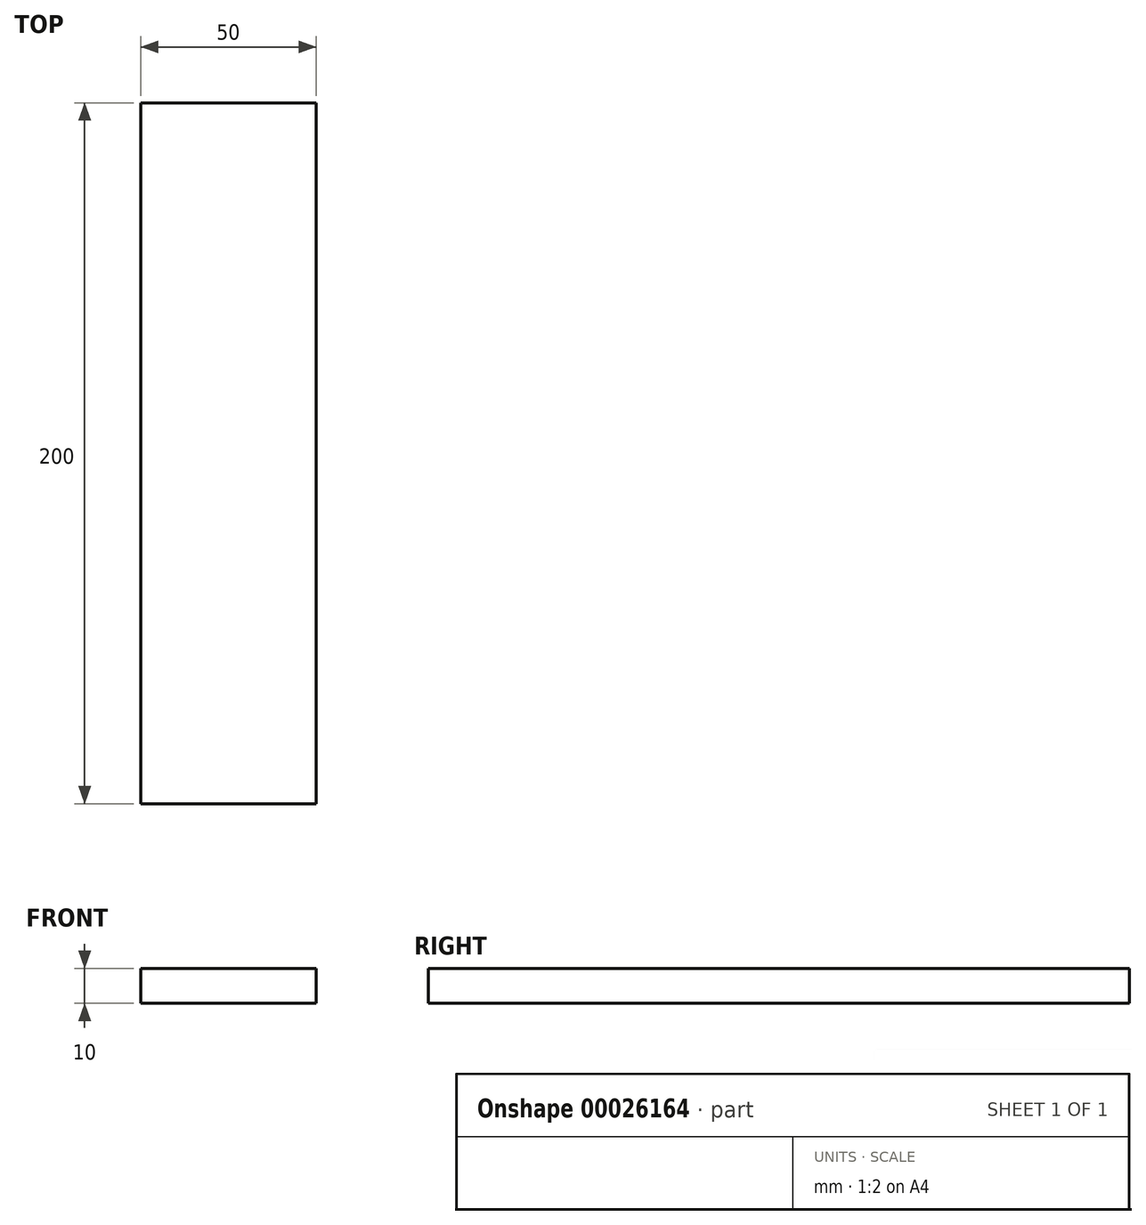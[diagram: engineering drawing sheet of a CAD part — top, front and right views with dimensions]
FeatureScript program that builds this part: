
annotation { "Feature Type Name" : "Feature", "Feature Type Description" : "" }
export const myFeature = defineFeature(function(context is Context, id is Id, definition is map)
    precondition{}
    {
        {
            var Q0;
            Q0=qCreatedBy(makeId("Top.planeOp"),FACE);
            var sketch = newSketch(context, id + "F0", { "sketchPlane" : qUnion([Q0])});
            skLineSegment(sketch, "E0.rect.bottom", {"start": v(25, -100) * mm, "end": v(-25, -100) * mm});
            skLineSegment(sketch, "E0.rect.top", {"start": v(25, 100) * mm, "end": v(-25, 100) * mm});
            skLineSegment(sketch, "E0.rect.left", {"start": v(25, -100) * mm, "end": v(25, 100) * mm});
            skLineSegment(sketch, "E0.rect.right", {"start": v(-25, -100) * mm, "end": v(-25, 100) * mm});
            skPoint(sketch, "E0.rect.middle", {"position": v(0, 0) * mm});
            skSolve(sketch);
        }
        {
            var Q0;
            Q0=makeQuery(id+"F0.imprint","IMPRINT",FACE,{"disambiguationData":[TD([[makeQuery(id+"F0.imprint","IMPRINT",EDGE,{"derivedFrom":sQuery(id+"F0.wireOp",EDGE,"E0.rect.bottom")}),-1.0]])]});
            extrude(context, id + "F1", {"entities" : qUnion([Q0]), "depth" : 10 * mm});
        }
    });
